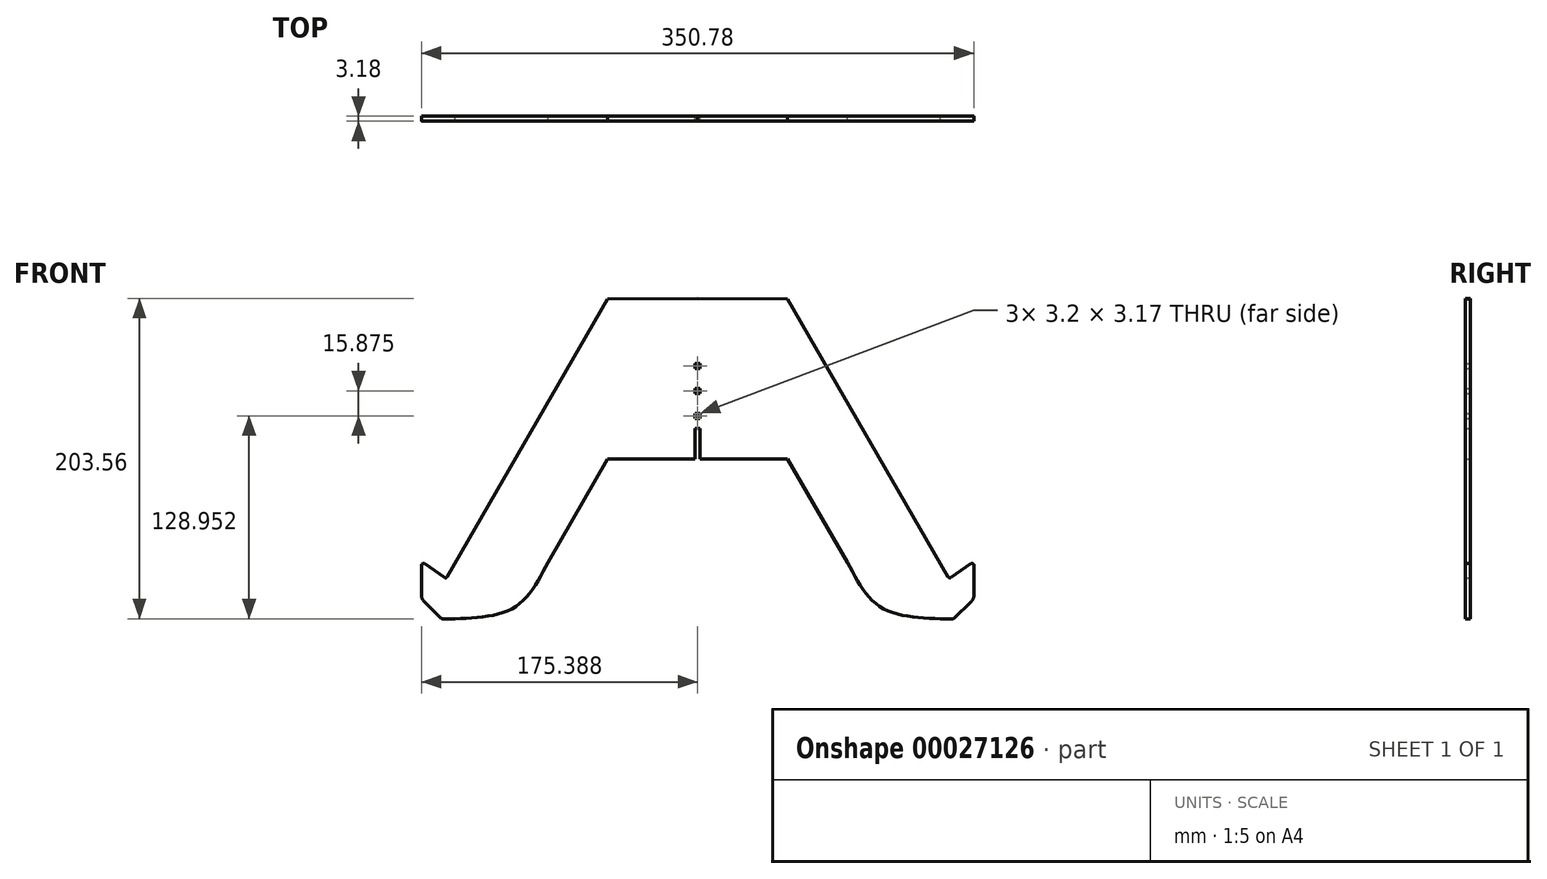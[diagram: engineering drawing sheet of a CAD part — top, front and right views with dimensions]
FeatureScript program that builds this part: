
annotation { "Feature Type Name" : "Feature", "Feature Type Description" : "" }
export const myFeature = defineFeature(function(context is Context, id is Id, definition is map)
    precondition{}
    {
        {
            var Q0;
            Q0=qCreatedBy(makeId("Front.planeOp"),FACE);
            var sketch = newSketch(context, id + "F0", { "sketchPlane" : qUnion([Q0])});
            skLineSegment(sketch, "E0.bottom", {"start": v(-67.64, 88.9) * mm, "end": v(-10.5, 89.26) * mm});
            skLineSegment(sketch, "E1", {"start": v(-67.64, 88.9) * mm, "end": v(-169.57, -87.65) * mm});
            skLineSegment(sketch, "E2", {"start": v(-171.4, -88.05) * mm, "end": v(-183.88, -79.31) * mm});
            skLineSegment(sketch, "E3", {"start": v(-185.88, -80.35) * mm, "end": v(-185.88, -88.06) * mm});
            skPoint(sketch, "E4.visualSharp", {"position": v(-170.26, -88.85) * mm});
            skArc(sketch, "E4.filletArc", {"start": v(-171.4, -88.05) * mm, "mid": v(-170.4, -88.25) * mm, "end": v(-169.57, -87.65) * mm});
            skPoint(sketch, "E5.visualSharp", {"position": v(-185.88, -77.91) * mm});
            skArc(sketch, "E5.filletArc", {"start": v(-183.88, -79.31) * mm, "mid": v(-185.2, -79.23) * mm, "end": v(-185.88, -80.35) * mm});
            skLineSegment(sketch, "E6", {"start": v(-185.88, -88.06) * mm, "end": v(-185.88, -99.62) * mm});
            skPoint(sketch, "E7.newPointA", {"position": v(-185.88, -114.3) * mm});
            skArc(sketch, "E7.filletArc", {"start": v(-185.88, -99.62) * mm, "mid": v(-185.48, -101.6) * mm, "end": v(-184.33, -103.28) * mm});
            skPoint(sketch, "E8.start.orphan", {"position": v(-61.95, 17.88) * mm});
            skPoint(sketch, "E9.end.orphan", {"position": v(-11.15, -39.67) * mm});
            skLineSegment(sketch, "E10", {"start": v(-105.58, -78.41) * mm, "end": v(-67.64, -12.7) * mm});
            skLineSegment(sketch, "E11", {"start": v(-67.64, -12.7) * mm, "end": v(-12.08, -12.7) * mm});
            skLineSegment(sketch, "E12", {"start": v(-12.08, -12.7) * mm, "end": v(-12.08, 0) * mm});
            skLineSegment(sketch, "E13.bottom", {"start": v(-10.5, 16.24) * mm, "end": v(-12.1, 16.24) * mm});
            skLineSegment(sketch, "E13.top", {"start": v(-10.5, 13.06) * mm, "end": v(-12.1, 13.06) * mm});
            skLineSegment(sketch, "E13.right", {"start": v(-12.1, 16.24) * mm, "end": v(-12.1, 13.06) * mm});
            skLineSegment(sketch, "E14.bottom", {"start": v(-10.5, 44.81) * mm, "end": v(-12.1, 44.81) * mm});
            skLineSegment(sketch, "E14.top", {"start": v(-10.5, 47.99) * mm, "end": v(-12.1, 47.99) * mm});
            skLineSegment(sketch, "E14.right", {"start": v(-12.1, 44.81) * mm, "end": v(-12.1, 47.99) * mm});
            skLineSegment(sketch, "E15.bottom", {"start": v(-10.5, 28.94) * mm, "end": v(-12.1, 28.94) * mm});
            skLineSegment(sketch, "E15.top", {"start": v(-10.5, 32.11) * mm, "end": v(-12.1, 32.11) * mm});
            skLineSegment(sketch, "E15.right", {"start": v(-12.1, 28.94) * mm, "end": v(-12.1, 32.11) * mm});
            skLineSegment(sketch, "E16", {"start": v(-10.5, 6.71) * mm, "end": v(-12.08, 6.71) * mm});
            skLineSegment(sketch, "E17", {"start": v(-12.08, 6.71) * mm, "end": v(-12.08, 0) * mm});
            skPoint(sketch, "E18.MirrorP", {"position": v(-9.83, -39.67) * mm});
            skLineSegment(sketch, "E19.MirrorCS", {"start": v(-10.5, 16.24) * mm, "end": v(-8.9, 16.24) * mm});
            skLineSegment(sketch, "E20.MirrorCS", {"start": v(-10.5, 13.06) * mm, "end": v(-8.9, 13.06) * mm});
            skLineSegment(sketch, "E21.MirrorCS", {"start": v(-10.5, 6.71) * mm, "end": v(-8.9, 6.71) * mm});
            skArc(sketch, "E22.MirrorCS", {"start": v(162.9, -79.31) * mm, "mid": v(164.21, -79.23) * mm, "end": v(164.9, -80.35) * mm});
            skLineSegment(sketch, "E23.MirrorCS", {"start": v(-8.9, 16.24) * mm, "end": v(-8.9, 13.06) * mm});
            skLineSegment(sketch, "E24.MirrorCS", {"start": v(-10.5, 28.94) * mm, "end": v(-8.9, 28.94) * mm});
            skArc(sketch, "E25.MirrorCS", {"start": v(164.9, -99.62) * mm, "mid": v(164.5, -101.6) * mm, "end": v(163.34, -103.28) * mm});
            skLineSegment(sketch, "E26.MirrorCS", {"start": v(150.42, -88.05) * mm, "end": v(162.9, -79.31) * mm});
            skLineSegment(sketch, "E27.MirrorCS", {"start": v(-8.9, 28.94) * mm, "end": v(-8.9, 32.11) * mm});
            skLineSegment(sketch, "E28.MirrorCS", {"start": v(-8.9, 44.81) * mm, "end": v(-8.9, 47.99) * mm});
            skLineSegment(sketch, "E29.MirrorCS", {"start": v(-10.5, 32.11) * mm, "end": v(-8.9, 32.11) * mm});
            skLineSegment(sketch, "E30.MirrorCS", {"start": v(-8.9, 6.71) * mm, "end": v(-8.9, 0) * mm});
            skArc(sketch, "E31.MirrorCS", {"start": v(150.42, -88.05) * mm, "mid": v(149.41, -88.25) * mm, "end": v(148.59, -87.65) * mm});
            skLineSegment(sketch, "E32.MirrorCS", {"start": v(-10.5, 44.81) * mm, "end": v(-8.9, 44.81) * mm});
            skLineSegment(sketch, "E33.MirrorCS", {"start": v(-10.5, 47.99) * mm, "end": v(-8.9, 47.99) * mm});
            skLineSegment(sketch, "E34.MirrorCS", {"start": v(164.9, -88.06) * mm, "end": v(164.9, -99.62) * mm});
            skLineSegment(sketch, "E35.MirrorCS", {"start": v(-8.9, -12.7) * mm, "end": v(-8.9, 0) * mm});
            skLineSegment(sketch, "E36.MirrorCS", {"start": v(164.9, -80.35) * mm, "end": v(164.9, -88.06) * mm});
            skPoint(sketch, "E37.MirrorP", {"position": v(149.28, -88.85) * mm});
            skPoint(sketch, "E38.MirrorP", {"position": v(40.97, 17.88) * mm});
            skPoint(sketch, "E39.MirrorP", {"position": v(164.9, -77.91) * mm});
            skLineSegment(sketch, "E40.MirrorCS", {"start": v(84.6, -78.41) * mm, "end": v(46.66, -12.7) * mm});
            skPoint(sketch, "E41.MirrorP", {"position": v(164.9, -114.3) * mm});
            skLineSegment(sketch, "E42.MirrorCS", {"start": v(46.66, 88.9) * mm, "end": v(-10.5, 89.26) * mm});
            skLineSegment(sketch, "E43.MirrorCS", {"start": v(46.66, 88.9) * mm, "end": v(148.59, -87.65) * mm});
            skLineSegment(sketch, "E44.MirrorCS", {"start": v(46.66, -12.7) * mm, "end": v(-8.9, -12.7) * mm});
            skPoint(sketch, "E45.orphan", {"position": v(-10.5, 29.67) * mm});
            skPoint(sketch, "E46.MirrorCS.end.orphan", {"position": v(-10.5, 31.46) * mm});
            skPoint(sketch, "E46.MirrorCS.start.orphan", {"position": v(-10.5, 44.16) * mm});
            skPoint(sketch, "E47.MirrorCS.end.orphan", {"position": v(-10.5, 16.24) * mm});
            skPoint(sketch, "E48.MirrorCS.end.orphan", {"position": v(-10.5, 5.7) * mm});
            skPoint(sketch, "E48.MirrorCS.start.orphan", {"position": v(-10.5, 12.04) * mm});
            skLineSegment(sketch, "E49", {"start": v(-164.69, -114.3) * mm, "end": v(-172.48, -114.3) * mm});
            skLineSegment(sketch, "E50", {"start": v(-184.33, -103.28) * mm, "end": v(-173.37, -113.94) * mm});
            skPoint(sketch, "E51.filletArc.start.orphan", {"position": v(-174.5, -112.75) * mm});
            skPoint(sketch, "E52.start.orphan", {"position": v(-173, -113.45) * mm});
            skPoint(sketch, "E53.visualSharp", {"position": v(-173, -114.3) * mm});
            skArc(sketch, "E53.filletArc", {"start": v(-173.37, -113.94) * mm, "mid": v(-172.96, -114.2) * mm, "end": v(-172.48, -114.3) * mm});
            skLineSegment(sketch, "E54.MirrorCS", {"start": v(143.7, -114.3) * mm, "end": v(151.5, -114.3) * mm});
            skArc(sketch, "E55.MirrorCS", {"start": v(152.38, -113.94) * mm, "mid": v(151.98, -114.2) * mm, "end": v(151.5, -114.3) * mm});
            skLineSegment(sketch, "E56.MirrorCS", {"start": v(163.34, -103.28) * mm, "end": v(152.38, -113.94) * mm});
            skPoint(sketch, "E57.MirrorCS.end.orphan", {"position": v(152.01, -113.45) * mm});
            skPoint(sketch, "E58.MirrorCS.end.orphan", {"position": v(153.52, -112.75) * mm});
            skFitSpline(sketch, "E59", {"points": [v(-164.69, -114.3) * mm, v(-126.53, -106.81) * mm, v(-105.58, -78.41) * mm], "startDerivative": vector(82.6, 3.46) * mm, "endDerivative": vector(35.23, 68.84) * mm});
            skFitSpline(sketch, "E60.MirrorCS", {"points": [v(143.7, -114.3) * mm, v(105.54, -106.81) * mm, v(84.6, -78.41) * mm], "startDerivative": vector(-82.6, 3.46) * mm, "endDerivative": vector(-35.23, 68.84) * mm});
            skLineSegment(sketch, "E61", {"start": v(-67.64, 82.55) * mm, "end": v(-64.47, 82.57) * mm});
            skLineSegment(sketch, "E62", {"start": v(-64.47, 82.57) * mm, "end": v(-64.42, 76.22) * mm});
            skLineSegment(sketch, "E63", {"start": v(-64.42, 76.22) * mm, "end": v(-67.64, 76.22) * mm});
            skLineSegment(sketch, "E64", {"start": v(-67.64, 82.55) * mm, "end": v(-67.64, 88.9) * mm});
            skLineSegment(sketch, "E65.1.0.0", {"start": v(-67.51, 69.85) * mm, "end": v(-67.51, 76.2) * mm});
            skLineSegment(sketch, "E65.1.0.1", {"start": v(-67.51, 69.85) * mm, "end": v(-64.34, 69.87) * mm});
            skLineSegment(sketch, "E65.1.0.2", {"start": v(-64.34, 69.87) * mm, "end": v(-64.3, 63.52) * mm});
            skLineSegment(sketch, "E65.1.0.3", {"start": v(-64.3, 63.52) * mm, "end": v(-67.51, 63.52) * mm});
            skLineSegment(sketch, "E65.2.0.0", {"start": v(-67.39, 57.15) * mm, "end": v(-67.39, 63.5) * mm});
            skLineSegment(sketch, "E65.2.0.1", {"start": v(-67.39, 57.15) * mm, "end": v(-64.21, 57.17) * mm});
            skLineSegment(sketch, "E65.2.0.2", {"start": v(-64.21, 57.17) * mm, "end": v(-64.17, 50.82) * mm});
            skLineSegment(sketch, "E65.2.0.3", {"start": v(-64.17, 50.82) * mm, "end": v(-67.39, 50.82) * mm});
            skLineSegment(sketch, "E65.3.0.0", {"start": v(-67.26, 44.45) * mm, "end": v(-67.26, 50.8) * mm});
            skLineSegment(sketch, "E65.3.0.1", {"start": v(-67.26, 44.45) * mm, "end": v(-64.08, 44.47) * mm});
            skLineSegment(sketch, "E65.3.0.2", {"start": v(-64.08, 44.47) * mm, "end": v(-64.04, 38.12) * mm});
            skLineSegment(sketch, "E65.3.0.3", {"start": v(-64.04, 38.12) * mm, "end": v(-67.26, 38.12) * mm});
            skLineSegment(sketch, "E65.4.0.0", {"start": v(-67.13, 31.75) * mm, "end": v(-67.13, 38.1) * mm});
            skLineSegment(sketch, "E65.4.0.1", {"start": v(-67.13, 31.75) * mm, "end": v(-63.96, 31.77) * mm});
            skLineSegment(sketch, "E65.4.0.2", {"start": v(-63.96, 31.77) * mm, "end": v(-63.92, 25.42) * mm});
            skLineSegment(sketch, "E65.4.0.3", {"start": v(-63.92, 25.42) * mm, "end": v(-67.13, 25.42) * mm});
            skLineSegment(sketch, "E65.5.0.0", {"start": v(-67, 19.05) * mm, "end": v(-67, 25.4) * mm});
            skLineSegment(sketch, "E65.5.0.1", {"start": v(-67, 19.05) * mm, "end": v(-63.83, 19.07) * mm});
            skLineSegment(sketch, "E65.5.0.2", {"start": v(-63.83, 19.07) * mm, "end": v(-63.8, 12.72) * mm});
            skLineSegment(sketch, "E65.5.0.3", {"start": v(-63.8, 12.72) * mm, "end": v(-67, 12.72) * mm});
            skLineSegment(sketch, "E65.6.0.0", {"start": v(-66.88, 6.35) * mm, "end": v(-66.88, 12.7) * mm});
            skLineSegment(sketch, "E65.6.0.1", {"start": v(-66.88, 6.35) * mm, "end": v(-63.7, 6.37) * mm});
            skLineSegment(sketch, "E65.6.0.2", {"start": v(-63.7, 6.37) * mm, "end": v(-63.66, 0.02) * mm});
            skLineSegment(sketch, "E65.6.0.3", {"start": v(-63.66, 0.02) * mm, "end": v(-66.88, 0.02) * mm});
            skLineSegment(sketch, "E65.7.0.0", {"start": v(-66.75, -6.35) * mm, "end": v(-66.75, 0) * mm});
            skLineSegment(sketch, "E65.7.0.1", {"start": v(-66.75, -6.35) * mm, "end": v(-63.58, -6.33) * mm});
            skLineSegment(sketch, "E65.7.0.2", {"start": v(-63.58, -6.33) * mm, "end": v(-63.54, -12.68) * mm});
            skLineSegment(sketch, "E65.7.0.3", {"start": v(-63.54, -12.68) * mm, "end": v(-66.75, -12.68) * mm});
            skLineSegment(sketch, "E65.direction1", {"start": v(-67.58, 76.22) * mm, "end": v(-67.51, 69.85) * mm, "construction": true});
            skLineSegment(sketch, "E66.MirrorCS", {"start": v(45.77, -6.35) * mm, "end": v(42.6, -6.33) * mm});
            skLineSegment(sketch, "E67.MirrorCS", {"start": v(46.28, 44.45) * mm, "end": v(43.1, 44.47) * mm});
            skLineSegment(sketch, "E68.MirrorCS", {"start": v(46.53, 69.85) * mm, "end": v(43.36, 69.87) * mm});
            skLineSegment(sketch, "E69.MirrorCS", {"start": v(46.02, 19.05) * mm, "end": v(42.85, 19.07) * mm});
            skLineSegment(sketch, "E70.MirrorCS", {"start": v(42.8, 12.72) * mm, "end": v(46.02, 12.72) * mm});
            skLineSegment(sketch, "E71.MirrorCS", {"start": v(43.32, 63.52) * mm, "end": v(46.53, 63.52) * mm});
            skLineSegment(sketch, "E72.MirrorCS", {"start": v(46.4, 57.15) * mm, "end": v(43.23, 57.17) * mm});
            skLineSegment(sketch, "E73.MirrorCS", {"start": v(45.9, 6.35) * mm, "end": v(42.72, 6.37) * mm});
            skLineSegment(sketch, "E74.MirrorCS", {"start": v(43.19, 50.82) * mm, "end": v(46.4, 50.82) * mm});
            skLineSegment(sketch, "E75.MirrorCS", {"start": v(42.68, 0.02) * mm, "end": v(45.9, 0.02) * mm});
            skLineSegment(sketch, "E76.MirrorCS", {"start": v(46.15, 31.75) * mm, "end": v(42.97, 31.77) * mm});
            skLineSegment(sketch, "E77.MirrorCS", {"start": v(43.44, 76.22) * mm, "end": v(46.66, 76.22) * mm});
            skLineSegment(sketch, "E78.MirrorCS", {"start": v(46.66, 82.55) * mm, "end": v(43.48, 82.57) * mm});
            skLineSegment(sketch, "E79.MirrorCS", {"start": v(43.06, 38.12) * mm, "end": v(46.28, 38.12) * mm});
            skLineSegment(sketch, "E80.MirrorCS", {"start": v(42.55, -12.68) * mm, "end": v(45.77, -12.68) * mm});
            skLineSegment(sketch, "E81.MirrorCS", {"start": v(42.93, 25.42) * mm, "end": v(46.15, 25.42) * mm});
            skLineSegment(sketch, "E82.MirrorCS", {"start": v(46.66, 82.55) * mm, "end": v(46.66, 88.9) * mm});
            skLineSegment(sketch, "E83.MirrorCS", {"start": v(46.53, 69.85) * mm, "end": v(46.53, 76.2) * mm});
            skLineSegment(sketch, "E84.MirrorCS", {"start": v(46.02, 19.05) * mm, "end": v(46.02, 25.4) * mm});
            skLineSegment(sketch, "E85.MirrorCS", {"start": v(42.6, -6.33) * mm, "end": v(42.55, -12.68) * mm});
            skLineSegment(sketch, "E86.MirrorCS", {"start": v(43.1, 44.47) * mm, "end": v(43.06, 38.12) * mm});
            skLineSegment(sketch, "E87.MirrorCS", {"start": v(43.36, 69.87) * mm, "end": v(43.32, 63.52) * mm});
            skLineSegment(sketch, "E88.MirrorCS", {"start": v(46.28, 44.45) * mm, "end": v(46.28, 50.8) * mm});
            skLineSegment(sketch, "E89.MirrorCS", {"start": v(45.77, -6.35) * mm, "end": v(45.77, 0) * mm});
            skLineSegment(sketch, "E90.MirrorCS", {"start": v(43.48, 82.57) * mm, "end": v(43.44, 76.22) * mm});
            skLineSegment(sketch, "E91.MirrorCS", {"start": v(46.15, 31.75) * mm, "end": v(46.15, 38.1) * mm});
            skLineSegment(sketch, "E92.MirrorCS", {"start": v(46.6, 76.22) * mm, "end": v(46.53, 69.85) * mm});
            skLineSegment(sketch, "E93.MirrorCS", {"start": v(42.97, 31.77) * mm, "end": v(42.93, 25.42) * mm});
            skLineSegment(sketch, "E94.MirrorCS", {"start": v(43.23, 57.17) * mm, "end": v(43.19, 50.82) * mm});
            skLineSegment(sketch, "E95.MirrorCS", {"start": v(42.72, 6.37) * mm, "end": v(42.68, 0.02) * mm});
            skLineSegment(sketch, "E96.MirrorCS", {"start": v(46.4, 57.15) * mm, "end": v(46.4, 63.5) * mm});
            skLineSegment(sketch, "E97.MirrorCS", {"start": v(45.9, 6.35) * mm, "end": v(45.9, 12.7) * mm});
            skLineSegment(sketch, "E98.MirrorCS", {"start": v(42.85, 19.07) * mm, "end": v(42.8, 12.72) * mm});
            skSolve(sketch);
        }
        {
            var Q0;
            Q0=makeQuery(id+"F0.imprint","IMPRINT",FACE,{"disambiguationData":[TD([[makeQuery(id+"F0.imprint","IMPRINT",EDGE,{"derivedFrom":sQuery(id+"F0.wireOp",EDGE,"3fdbb1ea-2064-493c-aa90-d8c0ab4ed308")}),1.0]])]});
            var Q1;
            Q1=makeQuery(id+"F0.imprint","IMPRINT",FACE,{"disambiguationData":[TD([[makeQuery(id+"F0.imprint","IMPRINT",EDGE,{"derivedFrom":sQuery(id+"F0.wireOp",EDGE,"E1")}),1.0]])]});
            var Q2;
            Q2=makeQuery(id+"F0.imprint","IMPRINT",FACE,{"disambiguationData":[TD([[makeQuery(id+"F0.imprint","IMPRINT",EDGE,{"derivedFrom":sQuery(id+"F0.wireOp",EDGE,"E0.bottom")}),-1.0]])]});
            var Q3;
            Q3=makeQuery(id+"F0.imprint","IMPRINT",FACE,{"disambiguationData":[TD([[makeQuery(id+"F0.imprint","IMPRINT",EDGE,{"derivedFrom":sQuery(id+"F0.wireOp",EDGE,"E22.MirrorCS")}),-1.0]])]});
            extrude(context, id + "F1", {"entities" : qUnion([Q0, Q1, Q2, Q3]), "depth" : 3.17 * mm});
        }
    });
